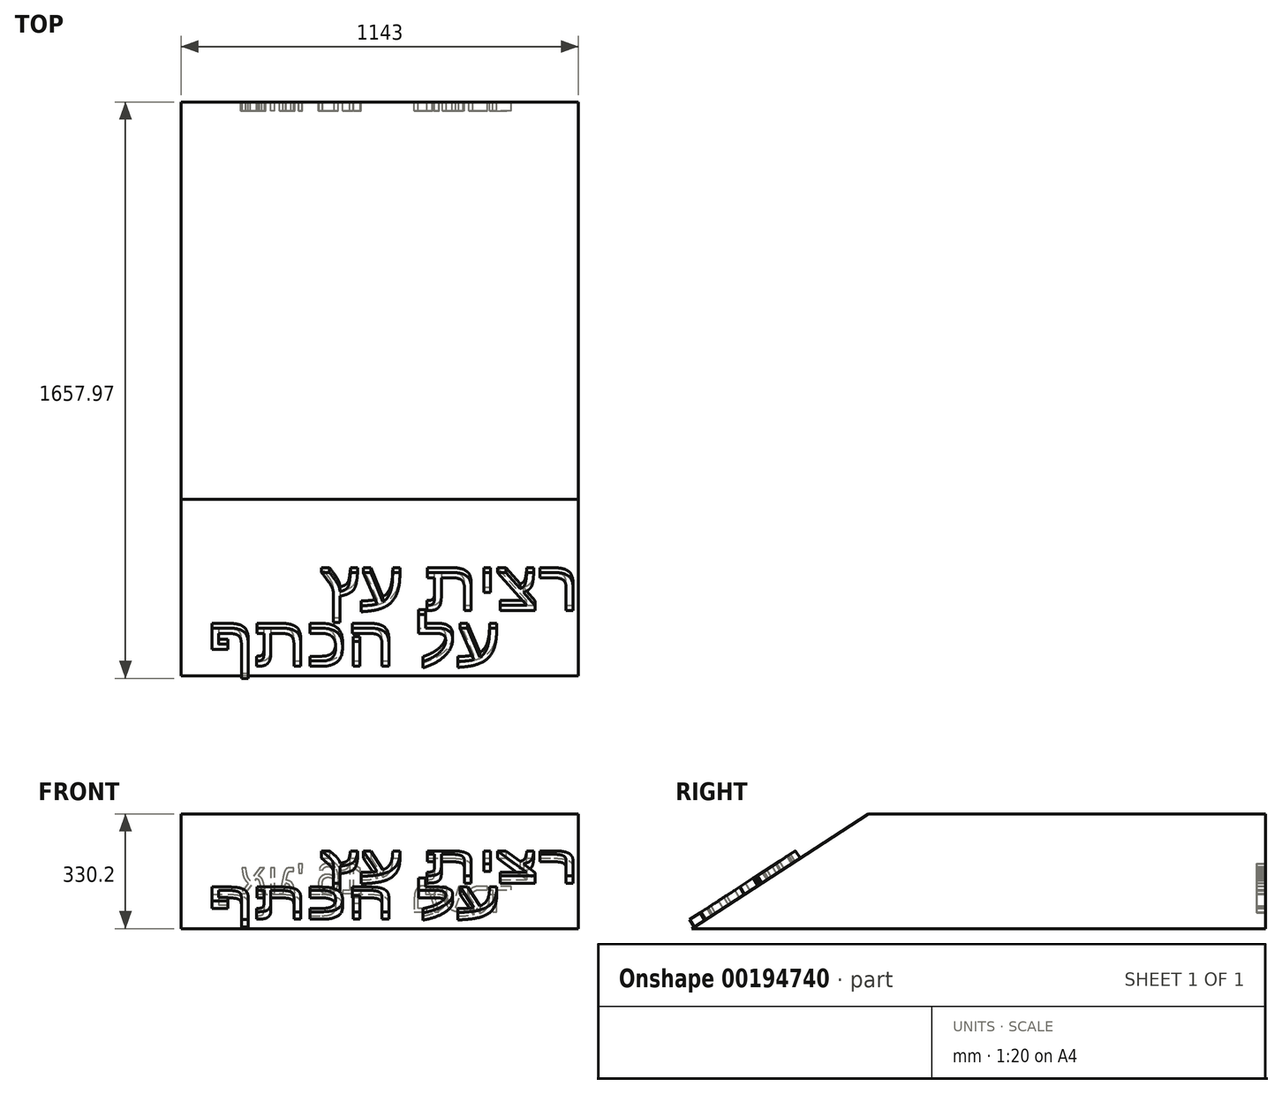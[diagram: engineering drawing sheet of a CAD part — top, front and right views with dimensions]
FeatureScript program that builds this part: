
annotation { "Feature Type Name" : "Feature", "Feature Type Description" : "" }
export const myFeature = defineFeature(function(context is Context, id is Id, definition is map)
    precondition{}
    {
        {
            var Q0;
            Q0=qCreatedBy(makeId("Right.planeOp"),FACE);
            var sketch = newSketch(context, id + "F0", { "sketchPlane" : qUnion([Q0])});
            skLineSegment(sketch, "E0", {"start": v(342.16, -668.62) * mm, "end": v(-800.84, -668.62) * mm});
            skLineSegment(sketch, "E1", {"start": v(-800.84, -668.62) * mm, "end": v(-1308.84, -998.82) * mm});
            skLineSegment(sketch, "E2", {"start": v(-1308.84, -998.82) * mm, "end": v(342.16, -998.82) * mm});
            skLineSegment(sketch, "E3", {"start": v(342.16, -998.82) * mm, "end": v(342.16, -668.62) * mm});
            skSolve(sketch);
        }
        {
            var Q0;
            Q0=makeQuery(id+"F0.imprint","IMPRINT",FACE,{"disambiguationData":[TD([[makeQuery(id+"F0.imprint","IMPRINT",EDGE,{"derivedFrom":sQuery(id+"F0.wireOp",EDGE,"E0")}),1.0]])]});
            extrude(context, id + "F1", {"entities" : qUnion([Q0]), "endBound" : BoundingType.SYMMETRIC, "depth" : 1143 * mm, "offsetDistance" : 25.4 * mm});
        }
        {
            var Q0;
            Q0=makeQuery(id+"F1.opExtrude","SWEPT_FACE",FACE,{"disambiguationData":[OSD([sQuery(id+"F0.wireOp",EDGE,"E1")])]});
            var sketch = newSketch(context, id + "F2", { "sketchPlane" : qUnion([Q0])});
            skText(sketch, "E4", { "text": "ץע תיצר", "fontName": "Arimo-Regular.ttf"});
            skText(sketch, "E5", { "text": "ףתכה לע", "fontName": "Arimo-Regular.ttf"});
            const initialGuessF2  = {"E4": [-0.16843, -1.40149, 1, 0, 0.15748], "E5": [-0.49708, -1.59242, 1, 0, 0.15748]};
            skSetInitialGuess(sketch, initialGuessF2);
            skSolve(sketch);
        }
        {
            var Q0;
            Q0 = qSketchRegion(id + "F2", true);
            extrude(context, id + "F3", {"entities" : qUnion([Q0]), "operationType" : NewBodyOperationType.ADD, "depth" : 25.4 * mm});
        }
        {
            var Q0;
            Q0=makeQuery(id+"F1.opExtrude","SWEPT_FACE",FACE,{"disambiguationData":[OSD([sQuery(id+"F0.wireOp",EDGE,"E3")])]});
            var sketch = newSketch(context, id + "F4", { "sketchPlane" : qUnion([Q0])});
            skText(sketch, "E6", { "text": "דרעמ", "fontName": "Arimo-Regular.ttf"});
            skText(sketch, "E7", { "text": "16 \'גוא", "fontName": "Arimo-Regular.ttf"});
            const initialGuessF4  = {"E6": [-0.38085, -0.95102, 1, 0, 0.0889], "E7": [0.0444, -0.89761, 1, 0, 0.0889]};
            skSetInitialGuess(sketch, initialGuessF4);
            skSolve(sketch);
        }
        {
            var Q0;
            Q0 = qSketchRegion(id + "F4", true);
            extrude(context, id + "F5", {"entities" : qUnion([Q0]), "operationType" : NewBodyOperationType.REMOVE, "oppositeDirection" : true, "depth" : 25.4 * mm});
        }
    });
